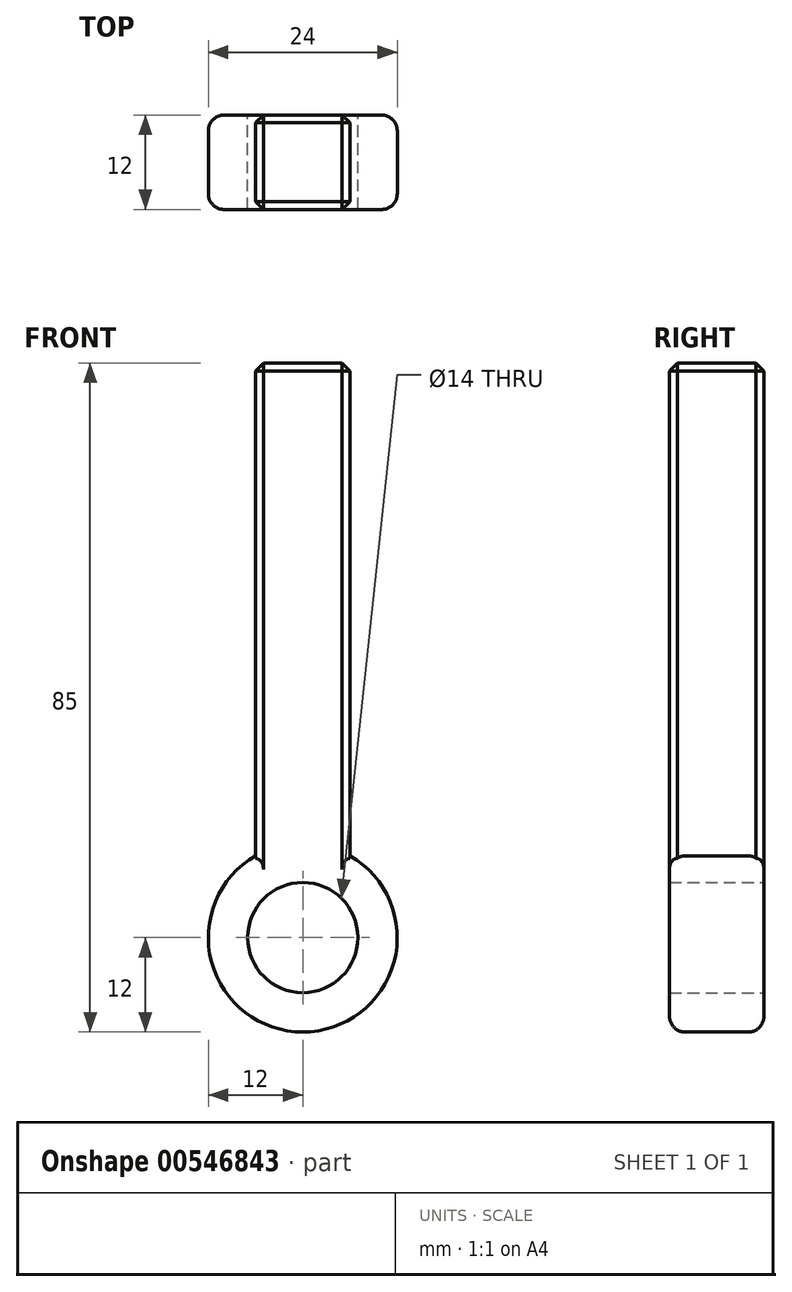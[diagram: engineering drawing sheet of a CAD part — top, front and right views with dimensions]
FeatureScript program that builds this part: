
annotation { "Feature Type Name" : "Feature", "Feature Type Description" : "" }
export const myFeature = defineFeature(function(context is Context, id is Id, definition is map)
    precondition{}
    {
        {
            var Q0;
            Q0=qCreatedBy(makeId("Top.planeOp"),FACE);
            var sketch = newSketch(context, id + "F0", { "sketchPlane" : qUnion([Q0])});
            skLineSegment(sketch, "E0.bottom", {"start": v(-6, 6) * mm, "end": v(6, 6) * mm});
            skLineSegment(sketch, "E0.top", {"start": v(-6, -6) * mm, "end": v(6, -6) * mm});
            skLineSegment(sketch, "E0.left", {"start": v(-6, 6) * mm, "end": v(-6, -6) * mm});
            skLineSegment(sketch, "E0.right", {"start": v(6, 6) * mm, "end": v(6, -6) * mm});
            skPoint(sketch, "E0.middle", {"position": v(0, 0) * mm});
            skSolve(sketch);
        }
        {
            var Q0;
            Q0=makeQuery(id+"F0.imprint","IMPRINT",FACE,{"disambiguationData":[TD([[makeQuery(id+"F0.imprint","IMPRINT",EDGE,{"derivedFrom":sQuery(id+"F0.wireOp",EDGE,"E0.bottom")}),-1.0]])]});
            extrude(context, id + "F1", {"entities" : qUnion([Q0]), "depth" : 65 * mm, "offsetDistance" : 25 * mm});
        }
        {
            var Q0;
            Q0=qCreatedBy(makeId("Front.planeOp"),FACE);
            var sketch = newSketch(context, id + "F2", { "sketchPlane" : qUnion([Q0])});
            skLineSegment(sketch, "E1", {"start": v(0, 0) * mm, "end": v(0, -8) * mm, "construction": true});
            skLineSegment(sketch, "E2", {"start": v(0, -8) * mm, "end": v(35, -8) * mm, "construction": true});
            skCircle(sketch, "E3", {"center": v(0, -8) * mm, "radius": 12 * mm});
            skCircle(sketch, "E4", {"center": v(0, -8) * mm, "radius": 7 * mm});
            skSolve(sketch);
        }
        {
            var Q0;
            Q0 = qSketchRegion(id + "F2", true);
            extrude(context, id + "F3", {"entities" : qUnion([Q0]), "operationType" : NewBodyOperationType.ADD, "depth" : 6 * mm, "offsetDistance" : 25 * mm, "hasSecondDirection" : true, "secondDirectionOppositeDirection" : true, "secondDirectionDepth" : 6 * mm});
        }
        {
            var Q0;
            Q0=makeQuery(id+"F3.opExtrude","CAP_EDGE",EDGE,{"disambiguationData":[OSD([sQuery(id+"F2.wireOp",EDGE,"E3")])],"isStart":false});
            var Q1;
            Q1=makeQuery(id+"F3.opExtrude","CAP_EDGE",EDGE,{"disambiguationData":[OSD([sQuery(id+"F2.wireOp",EDGE,"E3")])],"isStart":true});
            fillet(context, id + "F4", {"entities" : qUnion([Q0, Q1]), "radius" : 2 * mm, "tangentPropagation" : true, "allowEdgeOverflow" : false});
        }
        {
            var Q0;
            Q0=makeQuery(id+"F1.opExtrude","CAP_EDGE",EDGE,{"disambiguationData":[OSD([sQuery(id+"F0.wireOp",EDGE,"E0.top")])],"isStart":false});
            var Q1;
            Q1=makeQuery(id+"F1.opExtrude","CAP_EDGE",EDGE,{"disambiguationData":[OSD([sQuery(id+"F0.wireOp",EDGE,"E0.left")])],"isStart":false});
            var Q2;
            Q2=makeQuery(id+"F1.opExtrude","CAP_EDGE",EDGE,{"disambiguationData":[OSD([sQuery(id+"F0.wireOp",EDGE,"E0.bottom")])],"isStart":false});
            var Q3;
            Q3=makeQuery(id+"F1.opExtrude","CAP_EDGE",EDGE,{"disambiguationData":[OSD([sQuery(id+"F0.wireOp",EDGE,"E0.right")])],"isStart":false});
            var Q4;
            Q4=makeQuery(id+"F1.opExtrude","SWEPT_EDGE",EDGE,{"disambiguationData":[OSD([sQuery(id+"F0.wireOp",EDGE,"E0.top"),sQuery(id+"F0.wireOp",EDGE,"E0.right")])]});
            var Q5;
            Q5=makeQuery(id+"F1.opExtrude","SWEPT_EDGE",EDGE,{"disambiguationData":[OSD([sQuery(id+"F0.wireOp",EDGE,"E0.top"),sQuery(id+"F0.wireOp",EDGE,"E0.left")])]});
            var Q6;
            Q6=makeQuery(id+"F1.opExtrude","SWEPT_EDGE",EDGE,{"disambiguationData":[OSD([sQuery(id+"F0.wireOp",EDGE,"E0.bottom"),sQuery(id+"F0.wireOp",EDGE,"E0.right")])]});
            var Q7;
            Q7=makeQuery(id+"F1.opExtrude","SWEPT_EDGE",EDGE,{"disambiguationData":[OSD([sQuery(id+"F0.wireOp",EDGE,"E0.bottom"),sQuery(id+"F0.wireOp",EDGE,"E0.left")])]});
            chamfer(context, id + "F5", {"entities" : qUnion([Q0, Q1, Q2, Q3, Q4, Q5, Q6, Q7]), "width" : 1 * mm, "tangentPropagation" : true});
        }
    });
